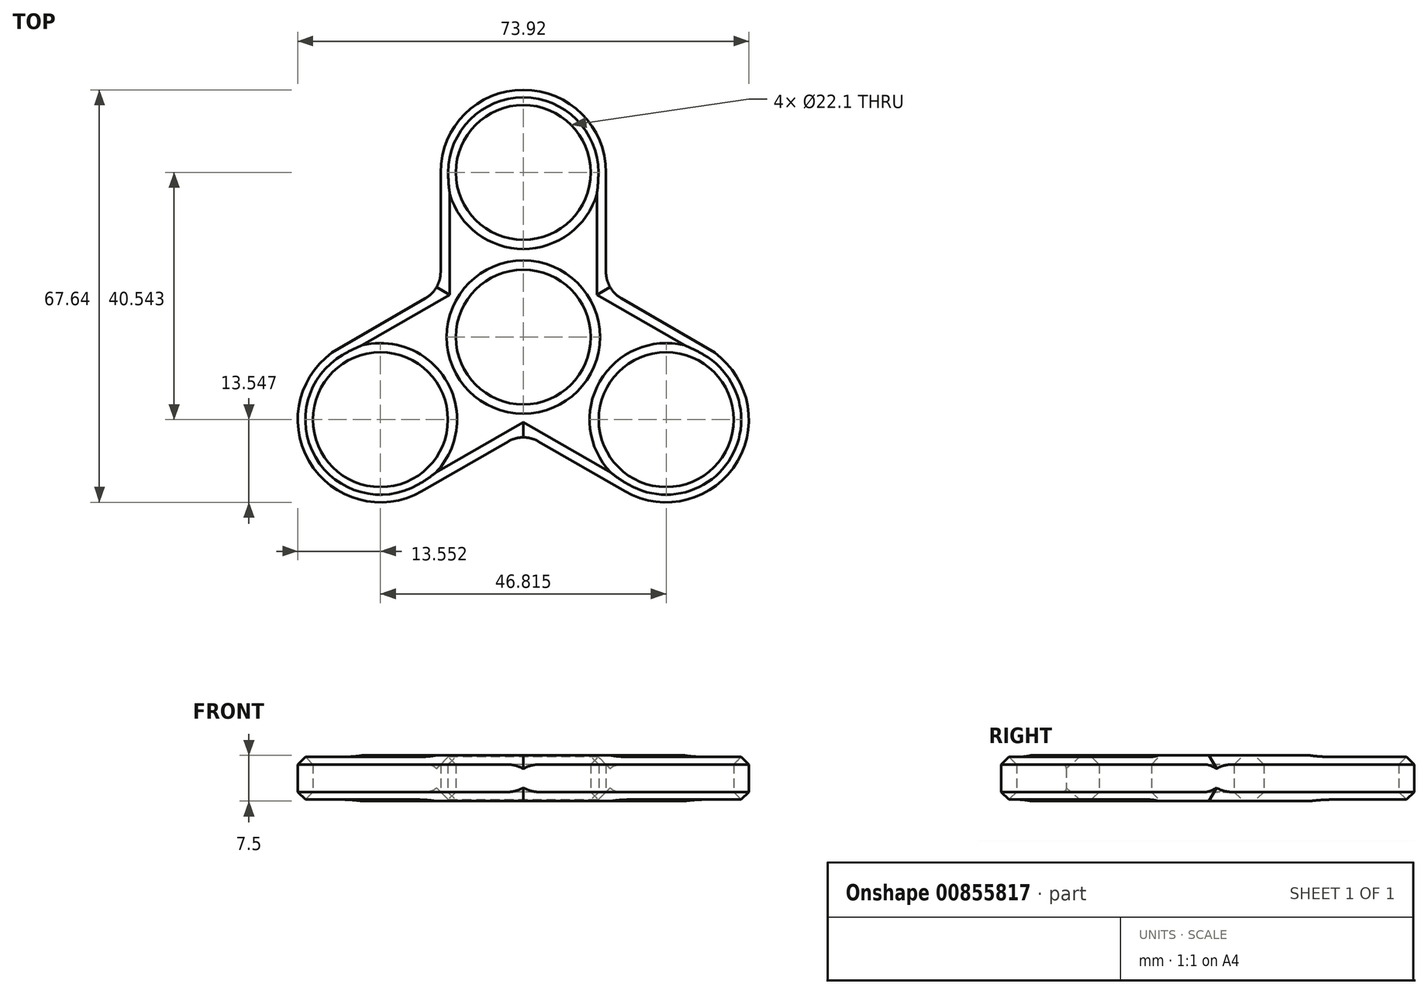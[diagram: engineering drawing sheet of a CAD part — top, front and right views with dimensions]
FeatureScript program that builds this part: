
annotation { "Feature Type Name" : "Feature", "Feature Type Description" : "" }
export const myFeature = defineFeature(function(context is Context, id is Id, definition is map)
    precondition{}
    {
        {
            var Q0;
            Q0=qCreatedBy(makeId("Top.planeOp"),FACE);
            var sketch = newSketch(context, id + "F0", { "sketchPlane" : qUnion([Q0])});
            skCircle(sketch, "E0", {"center": v(0, 0) * mm, "radius": 11.05 * mm});
            skCircle(sketch, "E1", {"center": v(0, 27) * mm, "radius": 11.05 * mm});
            skLineSegment(sketch, "E2", {"start": v(-13.55, 27) * mm, "end": v(-13.55, 7.8) * mm});
            skLineSegment(sketch, "E3", {"start": v(13.55, 27) * mm, "end": v(13.55, 7.8) * mm});
            skArc(sketch, "E4", {"start": v(-13.55, 27) * mm, "mid": v(0, 13.45) * mm, "end": v(13.55, 27) * mm, "construction": true});
            skArc(sketch, "E5", {"start": v(13.55, 27) * mm, "mid": v(0, 40.55) * mm, "end": v(-13.55, 27) * mm});
            skArc(sketch, "E6", {"start": v(-13.55, 0) * mm, "mid": v(0, -13.55) * mm, "end": v(13.55, 0) * mm, "construction": true});
            skArc(sketch, "E7", {"start": v(13.55, 0) * mm, "mid": v(0, 13.55) * mm, "end": v(-13.55, 0) * mm, "construction": true});
            skArc(sketch, "E8.1.0", {"start": v(-30.18, -1.8) * mm, "mid": v(-35.14, -20.32) * mm, "end": v(-16.63, -25.28) * mm});
            skCircle(sketch, "E8.1.1", {"center": v(-23.4, -13.54) * mm, "radius": 11.05 * mm});
            skLineSegment(sketch, "E8.1.2", {"start": v(-16.63, -25.28) * mm, "end": v(0, -15.68) * mm});
            skLineSegment(sketch, "E8.1.3", {"start": v(-30.18, -1.8) * mm, "end": v(-13.55, 7.8) * mm});
            skArc(sketch, "E8.2.0", {"start": v(16.63, -25.28) * mm, "mid": v(35.14, -20.32) * mm, "end": v(30.18, -1.8) * mm});
            skCircle(sketch, "E8.2.1", {"center": v(23.4, -13.54) * mm, "radius": 11.05 * mm});
            skLineSegment(sketch, "E8.2.2", {"start": v(30.18, -1.8) * mm, "end": v(13.55, 7.8) * mm});
            skLineSegment(sketch, "E8.2.3", {"start": v(16.63, -25.28) * mm, "end": v(0, -15.68) * mm});
            skPoint(sketch, "E8.center", {"position": v(0, -0.03) * mm});
            skLineSegment(sketch, "E9", {"start": v(-13.55, 7.8) * mm, "end": v(-13.55, 0) * mm, "construction": true});
            skLineSegment(sketch, "E10", {"start": v(-13.55, 7.8) * mm, "end": v(-6.8, 11.7) * mm, "construction": true});
            skLineSegment(sketch, "E11", {"start": v(0, -15.68) * mm, "end": v(-6.75, -11.78) * mm, "construction": true});
            skLineSegment(sketch, "E12", {"start": v(0, -15.68) * mm, "end": v(6.75, -11.78) * mm, "construction": true});
            skLineSegment(sketch, "E13", {"start": v(13.55, 7.8) * mm, "end": v(6.8, 11.7) * mm, "construction": true});
            skLineSegment(sketch, "E14", {"start": v(13.55, 7.8) * mm, "end": v(13.55, 0) * mm, "construction": true});
            skSolve(sketch);
        }
        {
            var Q0;
            Q0 = qSketchRegion(id + "F0", true);
            extrude(context, id + "F1", {"entities" : qUnion([Q0]), "depth" : 7.5 * mm, "offsetDistance" : 25 * mm});
        }
        {
            var Q0;
            Q0=makeQuery(id+"F1.opExtrude","CAP_EDGE",EDGE,{"disambiguationData":[OSD([sQuery(id+"F0.wireOp",EDGE,"E8.1.2")])],"isStart":false});
            var Q1;
            Q1=makeQuery(id+"F1.opExtrude","CAP_EDGE",EDGE,{"disambiguationData":[OSD([sQuery(id+"F0.wireOp",EDGE,"E2")])],"isStart":false});
            var Q2;
            Q2=makeQuery(id+"F1.opExtrude","CAP_EDGE",EDGE,{"disambiguationData":[OSD([sQuery(id+"F0.wireOp",EDGE,"E8.2.3")])],"isStart":false});
            var Q3;
            Q3=makeQuery(id+"F1.opExtrude","CAP_EDGE",EDGE,{"disambiguationData":[OSD([sQuery(id+"F0.wireOp",EDGE,"E8.1.1")])],"isStart":false});
            var Q4;
            Q4=makeQuery(id+"F1.opExtrude","CAP_EDGE",EDGE,{"disambiguationData":[OSD([sQuery(id+"F0.wireOp",EDGE,"E0")])],"isStart":false});
            var Q5;
            Q5=makeQuery(id+"F1.opExtrude","CAP_EDGE",EDGE,{"disambiguationData":[OSD([sQuery(id+"F0.wireOp",EDGE,"E1")])],"isStart":false});
            var Q6;
            Q6=makeQuery(id+"F1.opExtrude","CAP_EDGE",EDGE,{"disambiguationData":[OSD([sQuery(id+"F0.wireOp",EDGE,"E8.2.1")])],"isStart":false});
            var Q7;
            Q7=makeQuery(id+"F1.opExtrude","CAP_EDGE",EDGE,{"disambiguationData":[OSD([sQuery(id+"F0.wireOp",EDGE,"E2")])],"isStart":true});
            var Q8;
            Q8=makeQuery(id+"F1.opExtrude","CAP_EDGE",EDGE,{"disambiguationData":[OSD([sQuery(id+"F0.wireOp",EDGE,"E8.1.3")])],"isStart":true});
            var Q9;
            Q9=makeQuery(id+"F1.opExtrude","CAP_EDGE",EDGE,{"disambiguationData":[OSD([sQuery(id+"F0.wireOp",EDGE,"E8.2.3")])],"isStart":true});
            var Q10;
            Q10=makeQuery(id+"F1.opExtrude","CAP_EDGE",EDGE,{"disambiguationData":[OSD([sQuery(id+"F0.wireOp",EDGE,"E8.2.1")])],"isStart":true});
            var Q11;
            Q11=makeQuery(id+"F1.opExtrude","CAP_EDGE",EDGE,{"disambiguationData":[OSD([sQuery(id+"F0.wireOp",EDGE,"E0")])],"isStart":true});
            var Q12;
            Q12=makeQuery(id+"F1.opExtrude","CAP_EDGE",EDGE,{"disambiguationData":[OSD([sQuery(id+"F0.wireOp",EDGE,"E8.1.1")])],"isStart":true});
            var Q13;
            Q13=makeQuery(id+"F1.opExtrude","CAP_EDGE",EDGE,{"disambiguationData":[OSD([sQuery(id+"F0.wireOp",EDGE,"E1")])],"isStart":true});
            chamfer(context, id + "F2", {"entities" : qUnion([Q0, Q1, Q2, Q3, Q4, Q5, Q6, Q7, Q8, Q9, Q10, Q11, Q12, Q13]), "width" : 1.5 * mm, "tangentPropagation" : true});
        }
        {
            var Q0;
            Q0=makeQuery(id+"F1.opExtrude","SWEPT_EDGE",EDGE,{"disambiguationData":[OSD([sQuery(id+"F0.wireOp",EDGE,"E2"),sQuery(id+"F0.wireOp",EDGE,"E8.1.3")])]});
            var Q1;
            Q1=makeQuery(id+"F1.opExtrude","SWEPT_EDGE",EDGE,{"disambiguationData":[OSD([sQuery(id+"F0.wireOp",EDGE,"E3"),sQuery(id+"F0.wireOp",EDGE,"E8.2.2")])]});
            var Q2;
            Q2=makeQuery(id+"F1.opExtrude","SWEPT_EDGE",EDGE,{"disambiguationData":[OSD([sQuery(id+"F0.wireOp",EDGE,"E8.1.2"),sQuery(id+"F0.wireOp",EDGE,"E8.2.3")])]});
            fillet(context, id + "F3", {"entities" : qUnion([Q0, Q1, Q2]), "radius" : 5 * mm, "tangentPropagation" : true, "allowEdgeOverflow" : false});
        }
    });
